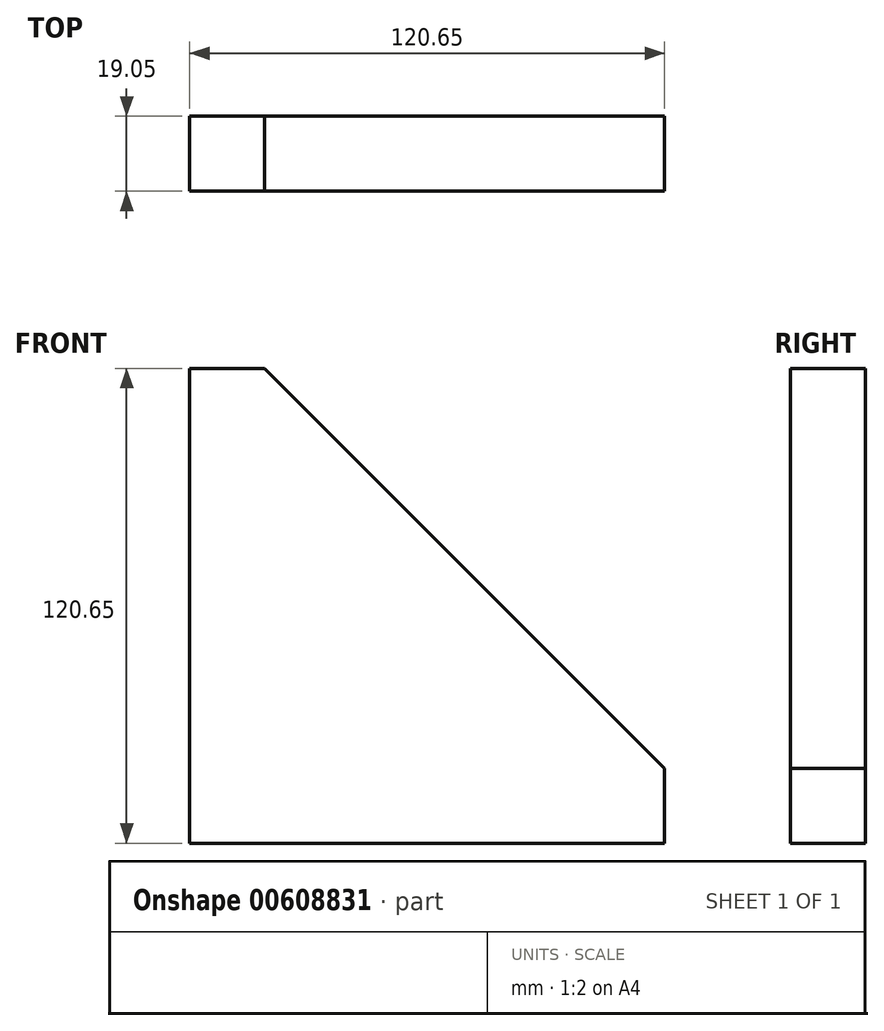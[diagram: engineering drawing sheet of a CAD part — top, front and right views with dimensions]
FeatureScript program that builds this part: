
annotation { "Feature Type Name" : "Feature", "Feature Type Description" : "" }
export const myFeature = defineFeature(function(context is Context, id is Id, definition is map)
    precondition{}
    {
        {
            var Q0;
            Q0=qCreatedBy(makeId("Front.planeOp"),FACE);
            var sketch = newSketch(context, id + "F0", { "sketchPlane" : qUnion([Q0])});
            skLineSegment(sketch, "E0", {"start": v(0, 0) * mm, "end": v(0, 120.65) * mm});
            skLineSegment(sketch, "E1", {"start": v(0, 120.65) * mm, "end": v(19.05, 120.65) * mm});
            skLineSegment(sketch, "E2", {"start": v(19.05, 120.65) * mm, "end": v(120.65, 19.05) * mm});
            skLineSegment(sketch, "E3", {"start": v(120.65, 19.05) * mm, "end": v(120.65, 0) * mm});
            skLineSegment(sketch, "E4", {"start": v(120.65, 0) * mm, "end": v(0, 0) * mm});
            skLineSegment(sketch, "E5", {"start": v(120.65, 19.05) * mm, "end": v(139.7, 0) * mm, "construction": true});
            skLineSegment(sketch, "E6", {"start": v(120.65, 0) * mm, "end": v(139.7, 0) * mm, "construction": true});
            skLineSegment(sketch, "E7", {"start": v(19.05, 120.65) * mm, "end": v(0, 139.7) * mm, "construction": true});
            skLineSegment(sketch, "E8", {"start": v(0, 139.7) * mm, "end": v(0, 120.65) * mm, "construction": true});
            skSolve(sketch);
        }
        {
            var Q0;
            Q0 = qSketchRegion(id + "F0", true);
            extrude(context, id + "F1", {"entities" : qUnion([Q0]), "depth" : 19.05 * mm, "offsetDistance" : 25.4 * mm});
        }
    });
